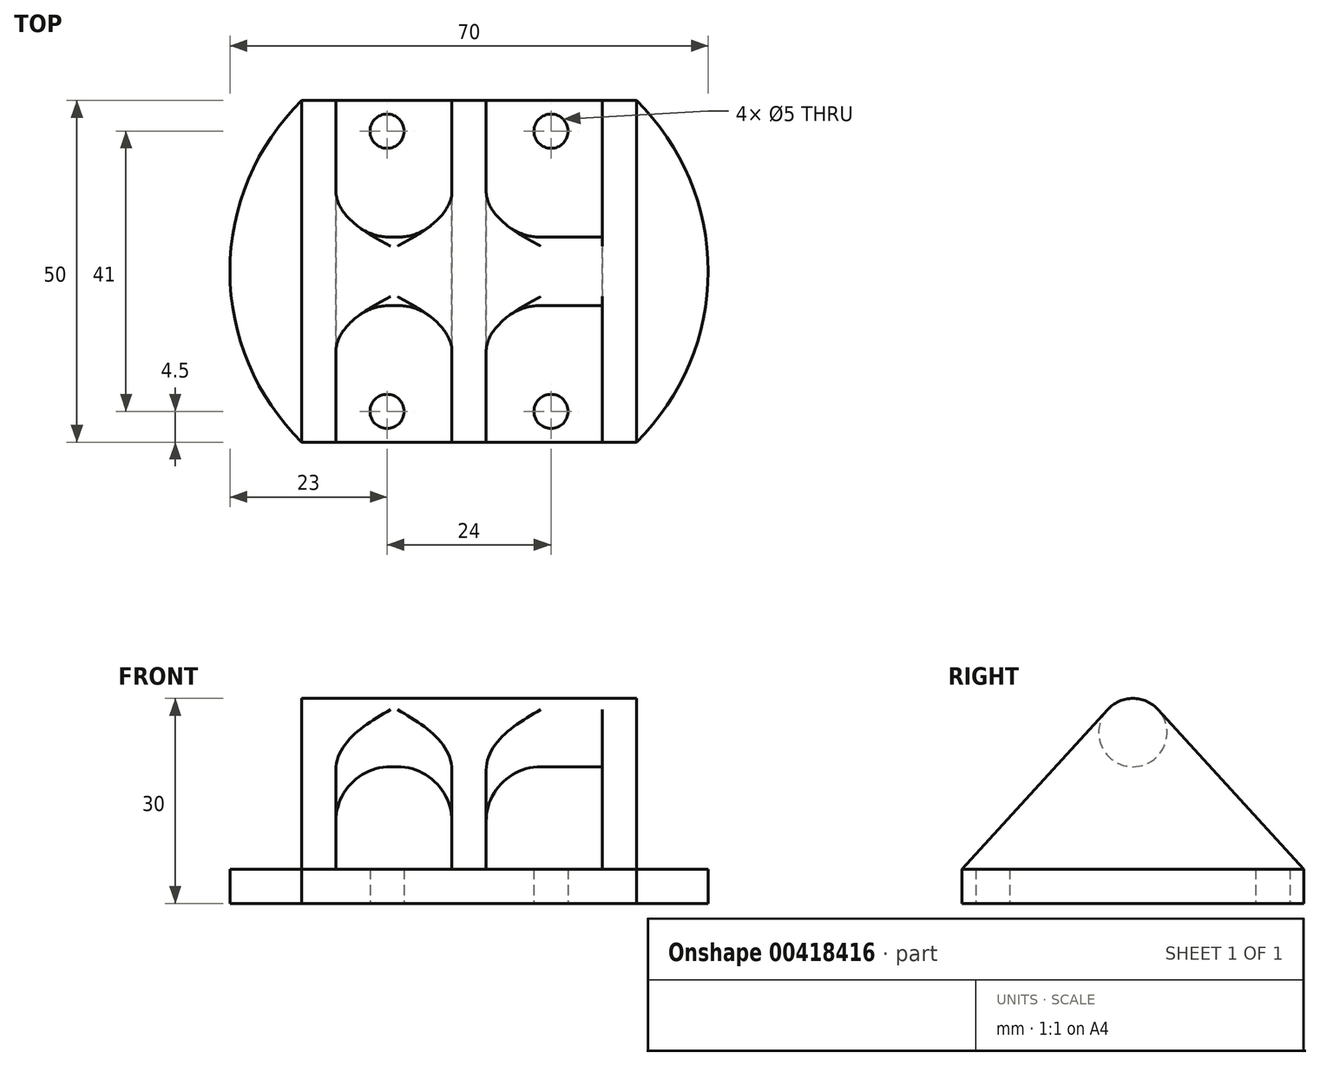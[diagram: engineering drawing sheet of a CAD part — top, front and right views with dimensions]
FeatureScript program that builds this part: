
annotation { "Feature Type Name" : "Feature", "Feature Type Description" : "" }
export const myFeature = defineFeature(function(context is Context, id is Id, definition is map)
    precondition{}
    {
        {
            var Q0;
            Q0=qCreatedBy(makeId("Top.planeOp"),FACE);
            var sketch = newSketch(context, id + "F0", { "sketchPlane" : qUnion([Q0])});
            skArc(sketch, "E0", {"start": v(-24.5, 25) * mm, "mid": v(-35, 0) * mm, "end": v(-24.5, -25) * mm});
            skLineSegment(sketch, "E1", {"start": v(-24.5, 25) * mm, "end": v(24.5, 25) * mm});
            skLineSegment(sketch, "E2", {"start": v(-24.5, -25) * mm, "end": v(24.5, -25) * mm});
            skArc(sketch, "E3.trimOffspring", {"start": v(24.5, -25) * mm, "mid": v(35, 0) * mm, "end": v(24.5, 25) * mm});
            skCircle(sketch, "E4", {"center": v(-12, -20.5) * mm, "radius": 2.5 * mm});
            skCircle(sketch, "E5", {"center": v(12, -20.5) * mm, "radius": 2.5 * mm});
            skCircle(sketch, "E6", {"center": v(12, 20.5) * mm, "radius": 2.5 * mm});
            skCircle(sketch, "E7", {"center": v(-12, 20.5) * mm, "radius": 2.5 * mm});
            skSolve(sketch);
        }
        {
            var Q0;
            Q0 = qSketchRegion(id + "F0", true);
            extrude(context, id + "F1", {"entities" : qUnion([Q0]), "depth" : 5 * mm});
        }
        {
            var Q0;
            Q0=makeQuery(id+"F1.opExtrude","CAP_FACE",FACE,{"disambiguationData":[OSD([sQuery(id+"F0.wireOp",EDGE,"E0"),sQuery(id+"F0.wireOp",EDGE,"E1"),sQuery(id+"F0.wireOp",EDGE,"E2"),sQuery(id+"F0.wireOp",EDGE,"E3.trimOffspring")])],"isStart":false});
            var sketch = newSketch(context, id + "F2", { "sketchPlane" : qUnion([Q0])});
            skLineSegment(sketch, "E8.bottom", {"start": v(-24.5, 25) * mm, "end": v(-19.5, 25) * mm});
            skLineSegment(sketch, "E8.top", {"start": v(-24.5, -25) * mm, "end": v(-19.5, -25) * mm});
            skLineSegment(sketch, "E8.left", {"start": v(-24.5, 25) * mm, "end": v(-24.5, -25) * mm});
            skLineSegment(sketch, "E8.right", {"start": v(-19.5, 25) * mm, "end": v(-19.5, -25) * mm});
            skLineSegment(sketch, "E9.bottom", {"start": v(24.5, 25) * mm, "end": v(19.5, 25) * mm});
            skLineSegment(sketch, "E9.top", {"start": v(24.5, -25) * mm, "end": v(19.5, -25) * mm});
            skLineSegment(sketch, "E9.left", {"start": v(24.5, 25) * mm, "end": v(24.5, -25) * mm});
            skLineSegment(sketch, "E9.right", {"start": v(19.5, 25) * mm, "end": v(19.5, -25) * mm});
            skLineSegment(sketch, "E10.bottom", {"start": v(-2.5, 25) * mm, "end": v(2.5, 25) * mm});
            skLineSegment(sketch, "E10.top", {"start": v(-2.5, -25) * mm, "end": v(2.5, -25) * mm});
            skLineSegment(sketch, "E10.left", {"start": v(-2.5, 25) * mm, "end": v(-2.5, -25) * mm});
            skLineSegment(sketch, "E10.right", {"start": v(2.5, 25) * mm, "end": v(2.5, -25) * mm});
            skSolve(sketch);
        }
        {
            var Q0;
            Q0 = qSketchRegion(id + "F2", true);
            extrude(context, id + "F3", {"entities" : qUnion([Q0]), "operationType" : NewBodyOperationType.ADD, "depth" : 25 * mm});
        }
        {
            var Q0;
            Q0=makeQuery(id+"F3.opExtrude","SWEPT_FACE",FACE,{"disambiguationData":[OSD([sQuery(id+"F2.wireOp",EDGE,"E8.left")])]});
            var sketch = newSketch(context, id + "F4", { "sketchPlane" : qUnion([Q0])});
            skArc(sketch, "E11", {"start": v(3.7, 28.37) * mm, "mid": v(0, 30) * mm, "end": v(-3.7, 28.37) * mm});
            skLineSegment(sketch, "E12", {"start": v(-25, 5) * mm, "end": v(-3.7, 28.37) * mm});
            skLineSegment(sketch, "E13", {"start": v(25, 5) * mm, "end": v(3.7, 28.37) * mm});
            skLineSegment(sketch, "E14", {"start": v(-25, 5) * mm, "end": v(-35, 5) * mm});
            skLineSegment(sketch, "E15", {"start": v(-35, 5) * mm, "end": v(-35, 40) * mm});
            skLineSegment(sketch, "E16", {"start": v(-35, 40) * mm, "end": v(35, 40) * mm});
            skLineSegment(sketch, "E17", {"start": v(35, 40) * mm, "end": v(35, 5) * mm});
            skLineSegment(sketch, "E18", {"start": v(35, 5) * mm, "end": v(25, 5) * mm});
            skSolve(sketch);
        }
        {
            var Q0;
            Q0 = qSketchRegion(id + "F4", true);
            extrude(context, id + "F5", {"entities" : qUnion([Q0]), "operationType" : NewBodyOperationType.REMOVE, "endBound" : BoundingType.THROUGH_ALL, "oppositeDirection" : true, "depth" : 25 * mm});
        }
        {
            var Q0;
            Q0=makeQuery(id+"F3.opExtrude","SWEPT_FACE",FACE,{"disambiguationData":[OSD([sQuery(id+"F2.wireOp",EDGE,"E9.right")])]});
            var sketch = newSketch(context, id + "F6", { "sketchPlane" : qUnion([Q0])});
            skCircle(sketch, "E19", {"center": v(0, 25) * mm, "radius": 5 * mm});
            skSolve(sketch);
        }
        {
            var Q0;
            Q0 = qSketchRegion(id + "F6", true);
            extrude(context, id + "F7", {"entities" : qUnion([Q0]), "operationType" : NewBodyOperationType.ADD, "depth" : 40 * mm});
        }
        {
            var Q0;
            Q0=makeQuery(id+"F7.boolean.opBoolean","INTERSECT",EDGE,{"derivedFrom":[makeQuery(id+"F3.opExtrude","SWEPT_FACE",FACE,{"disambiguationData":[OSD([sQuery(id+"F2.wireOp",EDGE,"E8.right")])]}),makeQuery(id+"F7.opExtrude","SWEPT_FACE",FACE,{"disambiguationData":[OSD([sQuery(id+"F6.wireOp",EDGE,"E19")])]})]});
            var Q1;
            Q1=makeQuery(id+"F7.boolean.opBoolean","INTERSECT",EDGE,{"derivedFrom":[makeQuery(id+"F3.opExtrude","SWEPT_FACE",FACE,{"disambiguationData":[OSD([sQuery(id+"F2.wireOp",EDGE,"E10.left")])]}),makeQuery(id+"F7.opExtrude","SWEPT_FACE",FACE,{"disambiguationData":[OSD([sQuery(id+"F6.wireOp",EDGE,"E19")])]})]});
            var Q2;
            Q2=makeQuery(id+"F7.boolean.opBoolean","INTERSECT",EDGE,{"derivedFrom":[makeQuery(id+"F3.opExtrude","SWEPT_FACE",FACE,{"disambiguationData":[OSD([sQuery(id+"F2.wireOp",EDGE,"E10.right")])]}),makeQuery(id+"F7.opExtrude","SWEPT_FACE",FACE,{"disambiguationData":[OSD([sQuery(id+"F6.wireOp",EDGE,"E19")])]})]});
            var Q3;
            Q3=makeQuery(id+"F7.opExtrude","CAP_EDGE",EDGE,{"disambiguationData":[OSD([sQuery(id+"F6.wireOp",EDGE,"E19")])],"isStart":true});
            fillet(context, id + "F8", {"entities" : qUnion([Q0, Q1, Q2, Q3]), "radius" : 8 * mm, "tangentPropagation" : true, "allowEdgeOverflow" : false});
        }
    });
